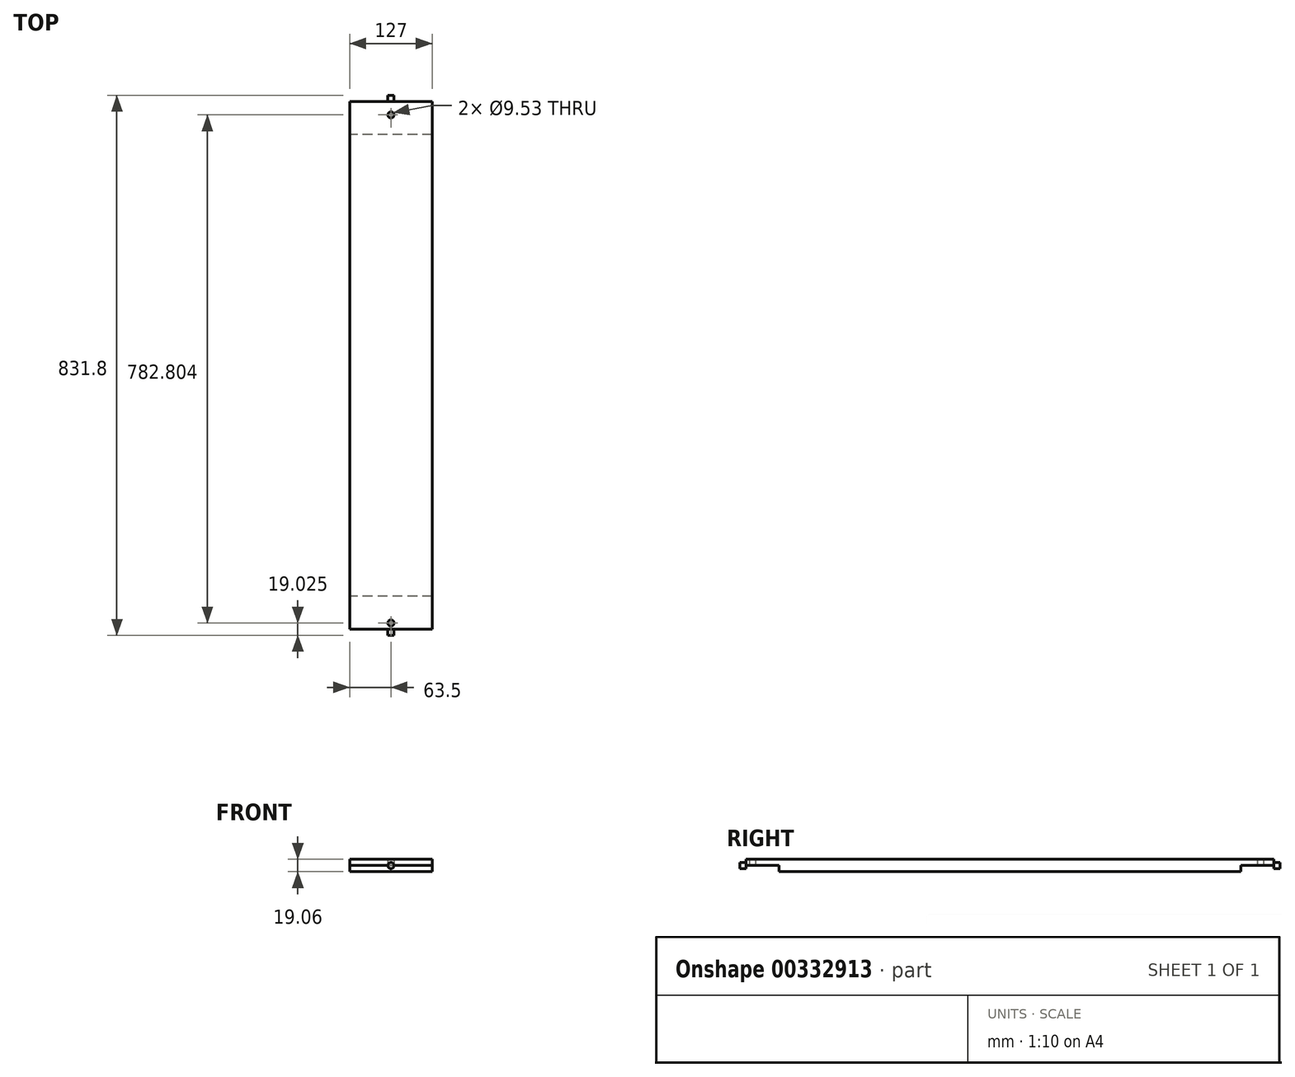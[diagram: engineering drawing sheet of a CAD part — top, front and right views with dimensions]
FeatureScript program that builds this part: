
annotation { "Feature Type Name" : "Feature", "Feature Type Description" : "" }
export const myFeature = defineFeature(function(context is Context, id is Id, definition is map)
    precondition{}
    {
        {
            var Q0;
            Q0=qCreatedBy(makeId("Right.planeOp"),FACE);
            var sketch = newSketch(context, id + "F0", { "sketchPlane" : qUnion([Q0])});
            skLineSegment(sketch, "E0.bottom", {"start": v(-355.6, -9.53) * mm, "end": v(355.6, -9.52) * mm});
            skLineSegment(sketch, "E0.top", {"start": v(-406.4, 9.52) * mm, "end": v(406.4, 9.53) * mm});
            skLineSegment(sketch, "E0.left", {"start": v(-406.4, 0) * mm, "end": v(-406.4, 9.52) * mm});
            skLineSegment(sketch, "E0.right", {"start": v(406.4, 0) * mm, "end": v(406.4, 9.53) * mm});
            skPoint(sketch, "E0.middle", {"position": v(0, 0) * mm});
            skLineSegment(sketch, "E1.bottom", {"start": v(-355.6, 0) * mm, "end": v(-406.4, 0) * mm});
            skLineSegment(sketch, "E1.left", {"start": v(-355.6, 0) * mm, "end": v(-355.6, -9.53) * mm});
            skLineSegment(sketch, "E2.bottom", {"start": v(406.4, 0) * mm, "end": v(355.6, 0) * mm});
            skLineSegment(sketch, "E2.right", {"start": v(355.6, 0) * mm, "end": v(355.6, -9.52) * mm});
            skSolve(sketch);
        }
        {
            var Q0;
            Q0=qSketchRegion(id+"F0",true);
            extrude(context, id + "F1", {"entities" : qUnion([Q0]), "depth" : 127 * mm});
        }
        {
            var Q0;
            Q0=makeQuery(id+"F1.opExtrude","SWEPT_FACE",FACE,{"disambiguationData":[OSD([sQuery(id+"F0.wireOp",EDGE,"E0.bottom")])]});
            var sketch = newSketch(context, id + "F2", { "sketchPlane" : qUnion([Q0])});
            skCircle(sketch, "E3", {"center": v(63.5, -385.93) * mm, "radius": 4.76 * mm});
            skCircle(sketch, "E4", {"center": v(63.5, 396.88) * mm, "radius": 4.76 * mm});
            skSolve(sketch);
        }
        {
            var Q0;
            Q0=qSketchRegion(id+"F2",true);
            extrude(context, id + "F3", {"entities" : qUnion([Q0]), "operationType" : NewBodyOperationType.REMOVE, "oppositeDirection" : true, "depth" : 25.4 * mm});
        }
        {
            var Q0;
            Q0=qCreatedBy(makeId("Front.planeOp"),FACE);
            cPlane(context, id + "F4", {"entities" : qUnion([Q0]), "cplaneType" : CPlaneType.OFFSET, "offset" : 406.37 * mm, "width" : 152.4 * mm, "height" : 152.4 * mm});
        }
        {
            var Q0;
            Q0=qCreatedBy(id+"F4.planeOp",FACE);
            var sketch = newSketch(context, id + "F5", { "sketchPlane" : qUnion([Q0])});
            skCircle(sketch, "E5", {"center": v(63.5, 0) * mm, "radius": 4.76 * mm});
            skSolve(sketch);
        }
        {
            var Q0;
            Q0=qSketchRegion(id+"F5",true);
            extrude(context, id + "F6", {"entities" : qUnion([Q0]), "depth" : 9.52 * mm});
        }
        {
            var Q0;
            Q0=qCreatedBy(makeId("Front.planeOp"),FACE);
            cPlane(context, id + "F7", {"entities" : qUnion([Q0]), "cplaneType" : CPlaneType.OFFSET, "offset" : 406.37 * mm, "oppositeDirection" : true, "width" : 152.4 * mm, "height" : 152.4 * mm});
        }
        {
            var Q0;
            Q0=qCreatedBy(id+"F7.planeOp",FACE);
            var sketch = newSketch(context, id + "F8", { "sketchPlane" : qUnion([Q0])});
            skCircle(sketch, "E6", {"center": v(63.5, 0) * mm, "radius": 4.76 * mm});
            skSolve(sketch);
        }
        {
            var Q0;
            Q0=qSketchRegion(id+"F8",true);
            extrude(context, id + "F9", {"entities" : qUnion([Q0]), "operationType" : NewBodyOperationType.ADD, "oppositeDirection" : true, "depth" : 9.52 * mm});
        }
    });
